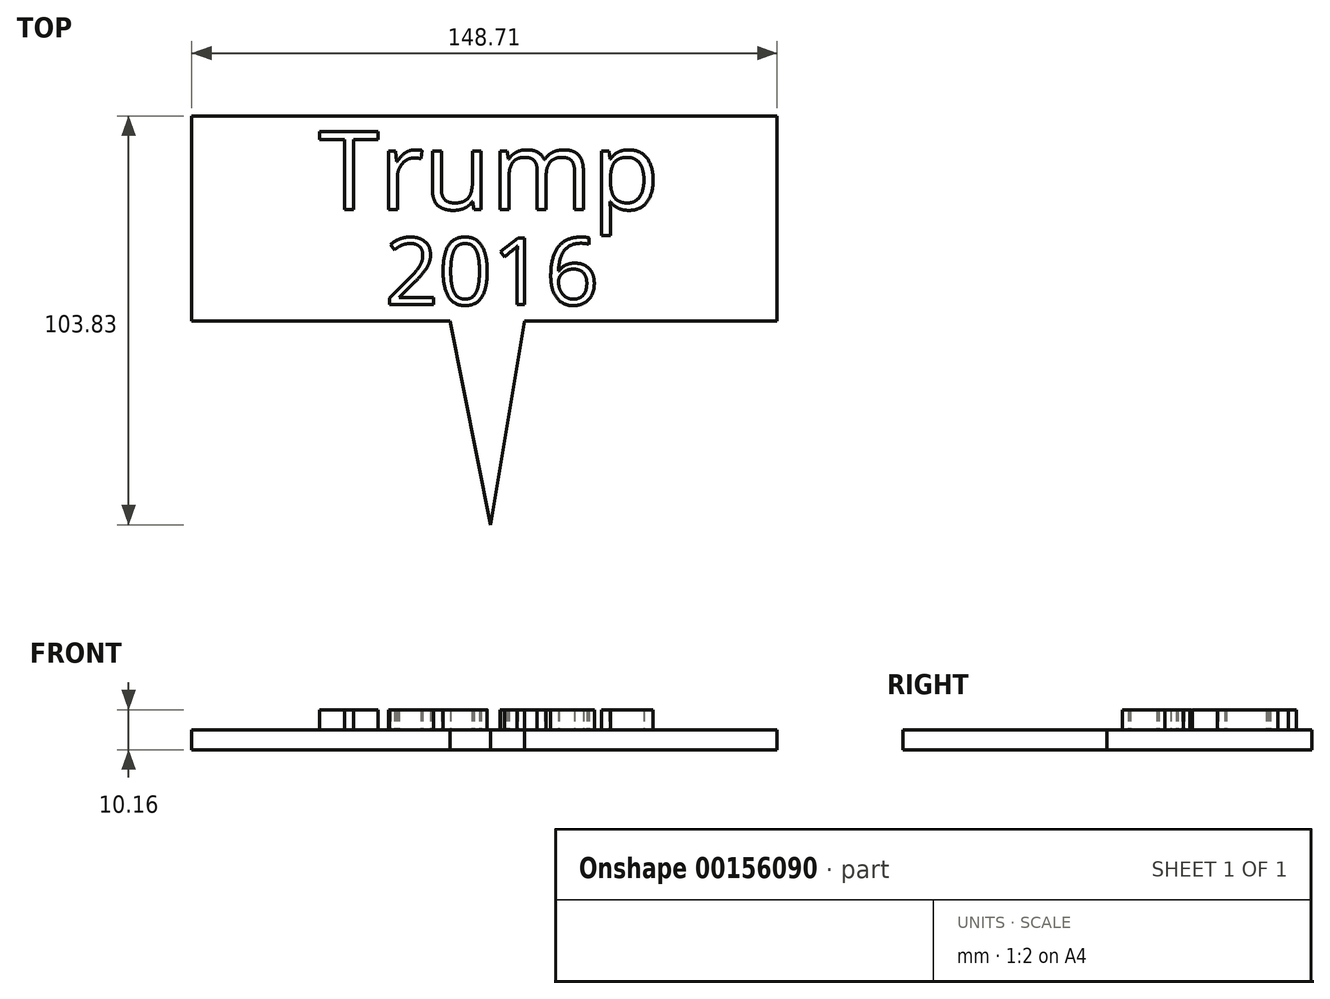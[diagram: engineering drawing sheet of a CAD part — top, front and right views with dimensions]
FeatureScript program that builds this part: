
annotation { "Feature Type Name" : "Feature", "Feature Type Description" : "" }
export const myFeature = defineFeature(function(context is Context, id is Id, definition is map)
    precondition{}
    {
        {
            var Q0;
            Q0=qCreatedBy(makeId("Top.planeOp"),FACE);
            var sketch = newSketch(context, id + "F0", { "sketchPlane" : qUnion([Q0])});
            skLineSegment(sketch, "E0", {"start": v(0, -51.77) * mm, "end": v(-10.27, 0) * mm});
            skLineSegment(sketch, "E1", {"start": v(-10.27, 0) * mm, "end": v(-75.9, 0) * mm});
            skLineSegment(sketch, "E2", {"start": v(-75.9, 0) * mm, "end": v(-75.9, 52.06) * mm});
            skLineSegment(sketch, "E3", {"start": v(-75.9, 52.06) * mm, "end": v(72.81, 52.06) * mm});
            skLineSegment(sketch, "E4", {"start": v(72.81, 52.06) * mm, "end": v(72.81, 0) * mm});
            skLineSegment(sketch, "E5", {"start": v(72.81, 0) * mm, "end": v(8.7, 0) * mm});
            skLineSegment(sketch, "E6", {"start": v(8.7, 0) * mm, "end": v(0, -51.77) * mm});
            skSolve(sketch);
        }
        {
            var Q0;
            Q0=makeQuery(id+"F0.imprint","IMPRINT",FACE,{"disambiguationData":[TD([[makeQuery(id+"F0.imprint","IMPRINT",EDGE,{"derivedFrom":sQuery(id+"F0.wireOp",EDGE,"E0")}),-1.0]])]});
            extrude(context, id + "F1", {"entities" : qUnion([Q0]), "depth" : 5.08 * mm});
        }
        {
            var Q0;
            Q0=makeQuery(id+"F1.opExtrude","CAP_FACE",FACE,{"disambiguationData":[OSD([sQuery(id+"F0.wireOp",EDGE,"E0"),sQuery(id+"F0.wireOp",EDGE,"E1"),sQuery(id+"F0.wireOp",EDGE,"E2"),sQuery(id+"F0.wireOp",EDGE,"E3"),sQuery(id+"F0.wireOp",EDGE,"E4"),sQuery(id+"F0.wireOp",EDGE,"E5"),sQuery(id+"F0.wireOp",EDGE,"E6")])],"isStart":false});
            var sketch = newSketch(context, id + "F2", { "sketchPlane" : qUnion([Q0])});
            skText(sketch, "E7", { "text": "Trump", "fontName": "OpenSans-Regular.ttf"});
            const initialGuessF2  = {"E7": [-0.04364, 0.02838, 1, 0, 0.01997]};
            skSetInitialGuess(sketch, initialGuessF2);
            skSolve(sketch);
        }
        {
            var Q0;
            Q0 = qSketchRegion(id + "F2", true);
            extrude(context, id + "F3", {"entities" : qUnion([Q0]), "operationType" : NewBodyOperationType.ADD, "depth" : 5.08 * mm});
        }
        {
            var Q0;
            {var subQ0=sQuery(id+"F0.wireOp",EDGE,"E2");var subQ1=sQuery(id+"F0.wireOp",EDGE,"E6");var subQ2=sQuery(id+"F0.wireOp",EDGE,"E4");var subQ3=sQuery(id+"F0.wireOp",EDGE,"E5");var subQ4=sQuery(id+"F0.wireOp",EDGE,"E1");var subQ5=sQuery(id+"F0.wireOp",EDGE,"E3");var subQ6=sQuery(id+"F0.wireOp",EDGE,"E0");Q0=makeQuery(id+"F3.boolean.opBoolean","SPLIT",FACE,{"disambiguationData":[TD([makeQuery(id+"F1.opExtrude","SWEPT_FACE",FACE,{"disambiguationData":[OSD([subQ6])]})])],"derivedFrom":makeQuery(id+"F1.opExtrude","CAP_FACE",FACE,{"disambiguationData":[OSD([subQ6,subQ4,subQ0,subQ5,subQ2,subQ3,subQ1])],"isStart":false})});}
            var sketch = newSketch(context, id + "F4", { "sketchPlane" : qUnion([Q0])});
            skText(sketch, "E8", { "text": "2016", "fontName": "OpenSans-Regular.ttf"});
            const initialGuessF4  = {"E8": [-0.02681, 0.00414, 1, 0, 0.01711]};
            skSetInitialGuess(sketch, initialGuessF4);
            skSolve(sketch);
        }
        {
            var Q0;
            Q0 = qSketchRegion(id + "F4", true);
            extrude(context, id + "F5", {"entities" : qUnion([Q0]), "operationType" : NewBodyOperationType.ADD, "depth" : 5.08 * mm});
        }
    });
